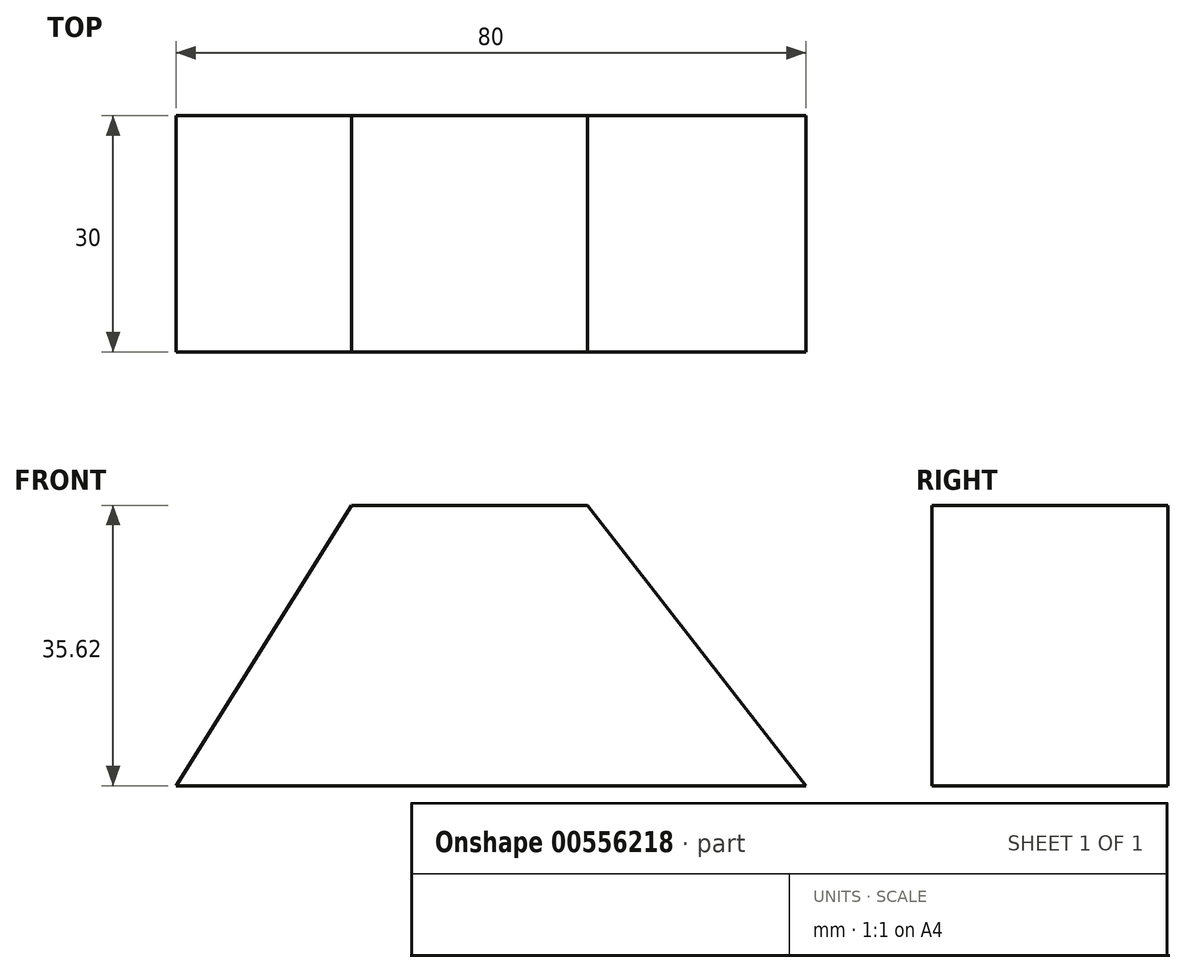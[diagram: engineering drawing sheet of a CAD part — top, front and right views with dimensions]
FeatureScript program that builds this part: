
annotation { "Feature Type Name" : "Feature", "Feature Type Description" : "" }
export const myFeature = defineFeature(function(context is Context, id is Id, definition is map)
    precondition{}
    {
        {
            var Q0;
            Q0=qCreatedBy(makeId("Front.planeOp"),FACE);
            var sketch = newSketch(context, id + "F0", { "sketchPlane" : qUnion([Q0])});
            skLineSegment(sketch, "E0", {"start": v(0, 0) * mm, "end": v(80, 0) * mm});
            skLineSegment(sketch, "E1", {"start": v(80, 0) * mm, "end": v(52.26, 35.62) * mm});
            skLineSegment(sketch, "E2", {"start": v(52.26, 35.62) * mm, "end": v(22.26, 35.62) * mm});
            skLineSegment(sketch, "E3", {"start": v(22.26, 35.62) * mm, "end": v(0, 0) * mm});
            skSolve(sketch);
        }
        {
            var Q0;
            Q0 = qSketchRegion(id + "F0", true);
            extrude(context, id + "F1", {"entities" : qUnion([Q0]), "depth" : 30 * mm, "offsetDistance" : 25 * mm});
        }
    });
